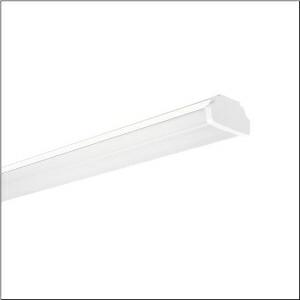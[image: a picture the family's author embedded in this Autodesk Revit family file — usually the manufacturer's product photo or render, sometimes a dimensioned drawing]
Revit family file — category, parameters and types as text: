
# Revit family: modario_31_gen_2_53bm812cv675c2_fe7d
name_source: partatom
category: Lighting Fixtures
units: mm (PartAtom-declared; Revit-internal decimal feet)

## family parameters
Cut with Voids When Loaded = No
Host = Face
Light Source = No
Part Type = Normal
Room Calculation Point = No
Round Connector Dimension = Use Diameter
Shared = No

## types (1)
- --- (1 x LED, 7670 lm, 42.1 W, 6500K)
    Apparent Load = 42 VA
    CIE Flux Codes = 47 80 95 93 100
    Color Rendering = 80
    Color Temperature = 6500K
    Default Elevation = 1800 mm
    Description = Modario 31 Gen.2, luminaire insert, of sheet steel, coil coated, white, length: 1.495mm, width: 81mm, height: 82mm, 5x system unit, system units: 299mm, LED rated luminous flux: 7.670lm, light colour: 865, SDCM (Standard Deviation of Colour Matching)MacAdam ≤ 3 SDCM (initial), control gear: ON/OFF Multilumen, CLOi, with plug, 3-pole, with phase selection, mains connection: 220..240V, AC, 50/60Hz, start of lifetime: 42W, end of service life: 50W, through-wiring accessed according to module size, primary optical cover: cover, of PMMA, light emission: direct distribution, primary light characteristic: symmetric, protection rating (complete): IP20, protection rating (LED compartment): IP50, insulation class (complete): insulation class I (protective earthing), certification: CE, ENEC, VDE, UKCA, impact resistance: IK03, permissible ambient temperature for indoor applications: -35..+50°C, corresponds to IFS (International Featured Standards) requirements for safety and quality in the food industry, reducing of maximum allowable ambient temperature of 5°C with ceiling mounting, IP40 when using the optional accessory 5TP9018, packaging unit: 1 piece
    Height = 92 mm
    Lamp = 1 x LED
    Lamp Light Flux = 7670 lm
    Lamp Power = 42.1 W
    Lamp count = 1
    Length = 1495 mm
    Luminous efficacy = 182 lm/W
    Manufacturer = Siteco
    ModVariant = No
    Model = 53BM812CV675C2
    Mounting Place = Ceiling
    Mounting Type = Pendant
    Number of Poles = 1
    OnlyDefault = Yes
    Power Factor = 1
    Product Name = Modario 31 Gen.2
    Product group = luminaire insert | ceiling pendant
    ProductGroupID = 901
    Protection Class = Protection class I
    Protection Degree = IP 20
    RLX_Detail_Level = 1
    RLX_Emergency_Light_Flux = 0 lm
    RLX_Emergency_Type = 0
    RLX_Emergency_Type_DB = No
    RlxData = <blob elided: 40061 chars, md5=a61a0b88>
    Socket = socket
    Standby Power = 0 W
    System Light Flux = 7670 lm
    System Power = 42 W
    Type Comments = factory setting: luminous flux: 100 % | (A | C | E) | 98 mA
    Type Image = l_1341886.jpg
    URL = http://relux.com
    VarID = @adj_040723
    Voltage = 0 V
    Weight = 0.00 kg
    Width = 81 mm

## geometry (parser evidence)
native form markers: Blend x4, Sweep x12
no freeform markers — native parametric forms only
